# Revit family: Kawneer - 5500 ISOWEB
name_source: partatom
category: Windows
revit_build: Autodesk Revit 2015 (Build: 20140905_0730(x64)
units: mm (PartAtom-declared; Revit-internal decimal feet)

## types (1)
- Kawneer - 5500 ISOWEB
    2- and 4-Sided Structural Glazed = No
    Assembly Code = B2020300
    CSI Masterformat Code = 08 51 13
    Color = Any
    Depth = 4"
    Description = An economical punched opening or horizontal ribbon window system suitable for low to mid rise applications. Utilizing the patented ISOWEB  polyamide thermal break for improved performance. The system may be adapted with the AA 900 operable window.
    Design Pressure = Fixed Double glazed  F-AW 80
Fixed Triple glazed  F-AW 75
    Frame Material = Aluminum - ASTM B 221 - 6063-T6 alloy and temper
    Function (Interior or Exterior) = Exterior, Interior
    Glass U-Factor = Fixed 0.36 to 0.12
    Glazing Thickness = 2"
    Hurricane Resistant Tested = product not tested
    Keywords = Fixed
    Manufacturer = KAWNEER
    Manufacturer Part Number = 5500 ISOWEB® Window
    Maximum Height = 0"
    Maximum Width = 0"
    Minimum Height = 0"
    Minimum Width = 0"
    Model = 5500 ISOWEB® Window
    Outside Glazed = No
    Overall U-Factor = Fixed Double Glazed 0.34
Fixed Triple Glazed 0.22
    Product data url = https://bimobject.com
    Short Description = Fixed Windows
    Style = Fixed
    Type Comments = 4" Fixed Window
    Type of Glazing = insulating
    URL = http://www.kawneer.com
    Width = 0"
    Window Pane = Glass

## geometry (parser evidence)
native form markers: Sweep x6
no freeform markers — native parametric forms only
